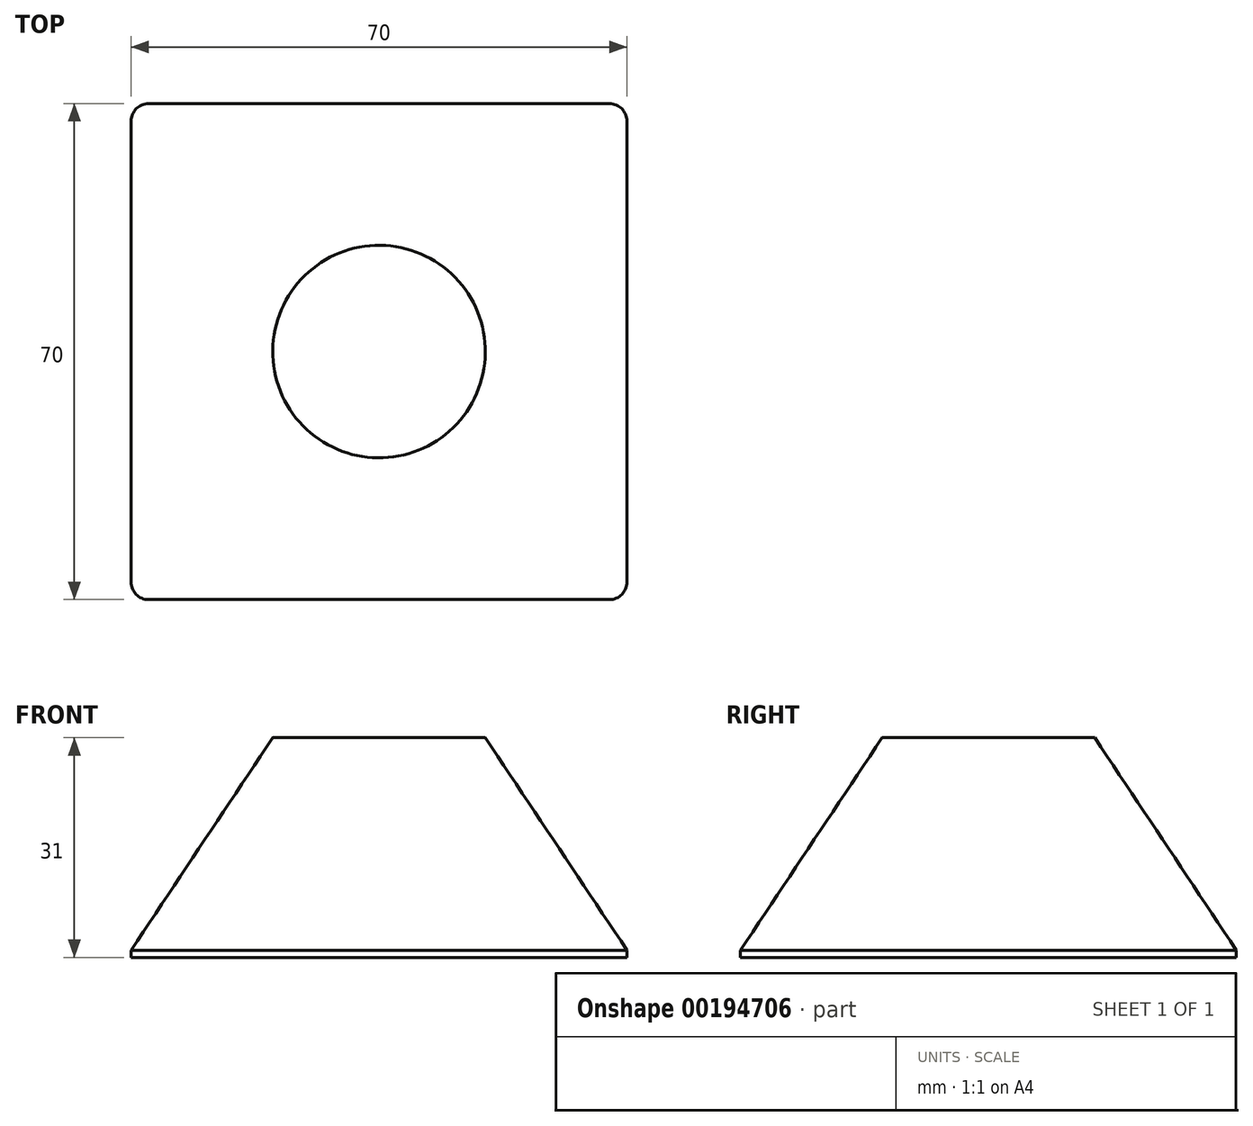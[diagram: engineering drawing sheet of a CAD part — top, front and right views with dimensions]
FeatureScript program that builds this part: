
annotation { "Feature Type Name" : "Feature", "Feature Type Description" : "" }
export const myFeature = defineFeature(function(context is Context, id is Id, definition is map)
    precondition{}
    {
        {
            var Q0;
            Q0=qCreatedBy(makeId("Top.planeOp"),FACE);
            var sketch = newSketch(context, id + "F0", { "sketchPlane" : qUnion([Q0])});
            skLineSegment(sketch, "E0.bottom", {"start": v(-32.5, -35) * mm, "end": v(32.5, -35) * mm});
            skLineSegment(sketch, "E0.top", {"start": v(-32.5, 35) * mm, "end": v(32.5, 35) * mm});
            skLineSegment(sketch, "E0.left", {"start": v(-35, -32.5) * mm, "end": v(-35, 32.5) * mm});
            skLineSegment(sketch, "E0.right", {"start": v(35, -32.5) * mm, "end": v(35, 32.5) * mm});
            skPoint(sketch, "E0.middle", {"position": v(0, 0) * mm});
            skPoint(sketch, "E1.visualSharp", {"position": v(-35, -35) * mm});
            skArc(sketch, "E1.filletArc", {"start": v(-35, -32.5) * mm, "mid": v(-34.27, -34.27) * mm, "end": v(-32.5, -35) * mm});
            skPoint(sketch, "E2.visualSharp", {"position": v(-35, 35) * mm});
            skArc(sketch, "E2.filletArc", {"start": v(-32.5, 35) * mm, "mid": v(-34.27, 34.27) * mm, "end": v(-35, 32.5) * mm});
            skPoint(sketch, "E3.visualSharp", {"position": v(35, 35) * mm});
            skArc(sketch, "E3.filletArc", {"start": v(35, 32.5) * mm, "mid": v(34.27, 34.27) * mm, "end": v(32.5, 35) * mm});
            skPoint(sketch, "E4.visualSharp", {"position": v(35, -35) * mm});
            skArc(sketch, "E4.filletArc", {"start": v(32.5, -35) * mm, "mid": v(34.27, -34.27) * mm, "end": v(35, -32.5) * mm});
            skSolve(sketch);
        }
        {
            var Q0;
            Q0=qCreatedBy(makeId("Top.planeOp"),FACE);
            cPlane(context, id + "F1", {"entities" : qUnion([Q0]), "cplaneType" : CPlaneType.OFFSET, "offset" : 30 * mm, "width" : 150 * mm, "height" : 150 * mm});
        }
        {
            var Q0;
            Q0=qCreatedBy(id+"F1.planeOp",FACE);
            var sketch = newSketch(context, id + "F2", { "sketchPlane" : qUnion([Q0])});
            skCircle(sketch, "E5", {"center": v(0, 0) * mm, "radius": 15 * mm});
            skSolve(sketch);
        }
        {
            var Q0;
            Q0=makeQuery(id+"F0.imprint","IMPRINT",FACE,{"disambiguationData":[TD([[makeQuery(id+"F0.imprint","IMPRINT",EDGE,{"derivedFrom":sQuery(id+"F0.wireOp",EDGE,"E0.bottom")}),1.0]])]});
            var Q1;
            Q1=makeQuery(id+"F2.imprint","IMPRINT",FACE,{"disambiguationData":[TD([[makeQuery(id+"F2.imprint","IMPRINT",EDGE,{"derivedFrom":sQuery(id+"F2.wireOp",EDGE,"E5")}),1.0]])]});
            loft(context, id + "F3", {"sheetProfilesArray" : [{ "sheetProfileEntities" : qUnion([Q0]) }, { "sheetProfileEntities" : qUnion([Q1]) }]});
        }
        {
            var Q0;
            Q0=makeQuery(id+"F3.opLoft","CAP_FACE",FACE,{"disambiguationData":[OSD([makeQuery(id+"F0.imprint","IMPRINT",FACE,{"disambiguationData":[TD([[makeQuery(id+"F0.imprint","IMPRINT",EDGE,{"derivedFrom":sQuery(id+"F0.wireOp",EDGE,"E0.bottom")}),1.0]])]})])],"isStart":true});
            extrude(context, id + "F4", {"entities" : qUnion([Q0]), "operationType" : NewBodyOperationType.ADD, "depth" : 1 * mm});
        }
    });
